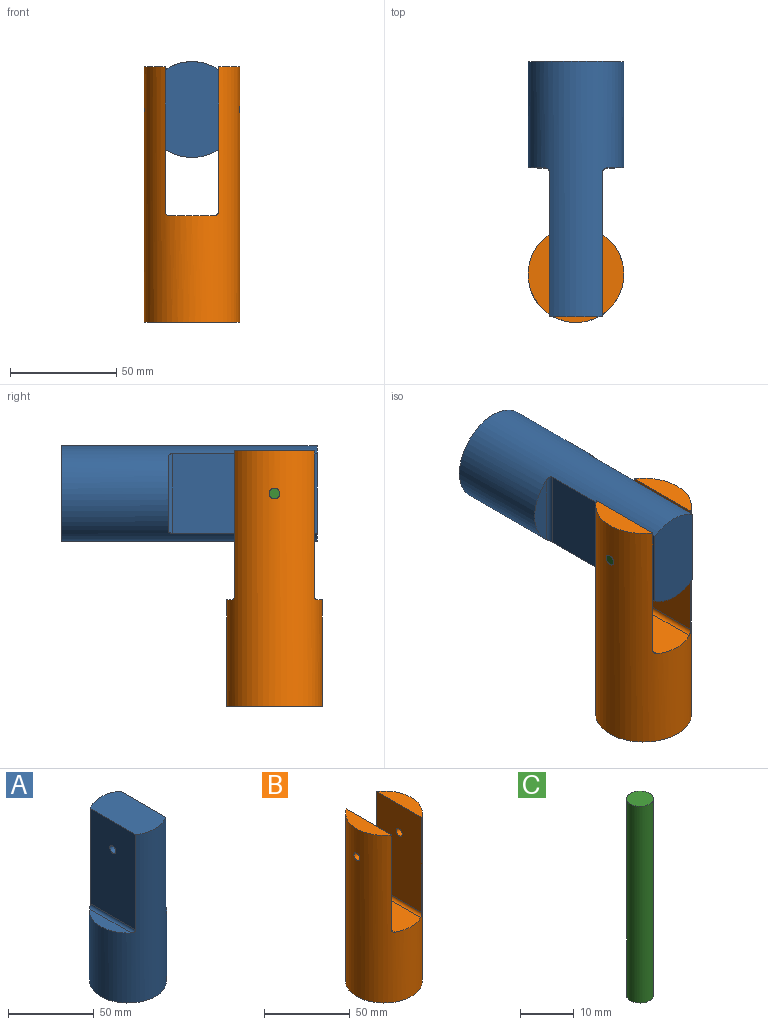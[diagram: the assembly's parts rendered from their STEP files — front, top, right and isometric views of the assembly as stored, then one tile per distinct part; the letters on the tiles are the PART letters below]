
ASSEMBLY  parts=3 mates=2
PART A: 12 faces, bbox 45x45x120 mm
  f0: plane 45x25mm, normal (0,0,1), area 1064.1mm2, adj f1,f3,f5
  f1: cylinder r=22.5mm len=120mm, axis (0,0,-1), area 10783.7mm2, adj f0,f2,f3,f4,f5,f6,f10,f11
  f2: plane 45x45mm, normal (0,0,-1), area 333.8mm2, adj f1,f7
  f3: plane 68x37.42mm, normal (-1,0,0), area 2524.7mm2, adj f0,f1,f9,f10
  f4: plane 34.41x8mm, normal (0,0,1), area 191.2mm2, adj f1,f10
  f5: plane 68x37.42mm, normal (1,0,0), area 2524.7mm2, adj f0,f1,f9,f11
  f6: plane 34.41x8mm, normal (0,0,1), area 191.2mm2, adj f1,f11
  f7: cylinder r=20mm len=40mm, axis (0,0,-1), area 4398.2mm2, adj f2,f8
  f8: plane 40x40mm, normal (0,0,-1), area 1256.6mm2, adj f7
  f9: cylinder r=2.5mm len=25mm, axis (1,0,0), area 392.7mm2, adj f3,f5
  f10: cylinder r=2mm len=37.42mm, axis (0,1,0), area 114.3mm2, adj f1,f3,f4
  f11: cylinder r=2mm len=37.42mm, axis (0,-1,0), area 114.3mm2, adj f1,f5,f6
PART B: 13 faces, bbox 45x45x120 mm
  f0: cylinder r=22.5mm len=120mm, axis (0,0,-1), area 13218.5mm2, adj f1,f2,f3,f4,f5,f6,f9,f10
  f1: plane 37.42x10mm, normal (0,0,1), area 263.2mm2, adj f0,f5
  f2: plane 37.42x10mm, normal (0,0,1), area 263.2mm2, adj f0,f4
  f3: plane 45x45mm, normal (0,0,-1), area 333.8mm2, adj f0,f7
  f4: plane 68x37.42mm, normal (1,0,0), area 2524.7mm2, adj f0,f2,f10,f11
  f5: plane 68x37.42mm, normal (-1,0,0), area 2524.7mm2, adj f0,f1,f9,f12
  f6: plane 45x21mm, normal (0,0,1), area 909.5mm2, adj f0,f11,f12
  f7: cylinder r=20mm len=40mm, axis (0,0,-1), area 4398.2mm2, adj f3,f8
  f8: plane 40x40mm, normal (0,0,-1), area 1256.6mm2, adj f7
  f9: cylinder r=2.5mm len=10mm, axis (1,0,0), area 156mm2, adj f0,f5
  f10: cylinder r=2.5mm len=10mm, axis (1,0,0), area 156mm2, adj f0,f4
  f11: cylinder r=2mm len=39.8mm, axis (0,-1,0), area 120.4mm2, adj f0,f4,f6
  f12: cylinder r=2mm len=39.8mm, axis (0,1,0), area 120.4mm2, adj f0,f5,f6
PART C: 3 faces, bbox 5x5x45 mm
  f0: cylinder r=2.5mm len=45mm, axis (0,0,-1), area 706.9mm2, adj f1,f2
  f1: plane 5x5mm, normal (0,0,1), area 19.6mm2, adj f0
  f2: plane 5x5mm, normal (0,0,-1), area 19.6mm2, adj f0
PLACE A rot(axis=(1,0,0),90deg) t=(-114.4,66.23,67.98)mm
PLACE B t=(-114.46,-33.77,-32.02)mm fixed
PLACE C rot(axis=(0,-1,0),90deg) t=(-91.9,-33.77,67.98)mm
MATE revolute A.f9 <-> C.f0  axis (1,0,0) through (-114.4,-33.77,67.98)mm
MATE fastened B.f9 <-> C.f0  axis (1,0,0) through (-91.9,-33.77,67.98)mm
